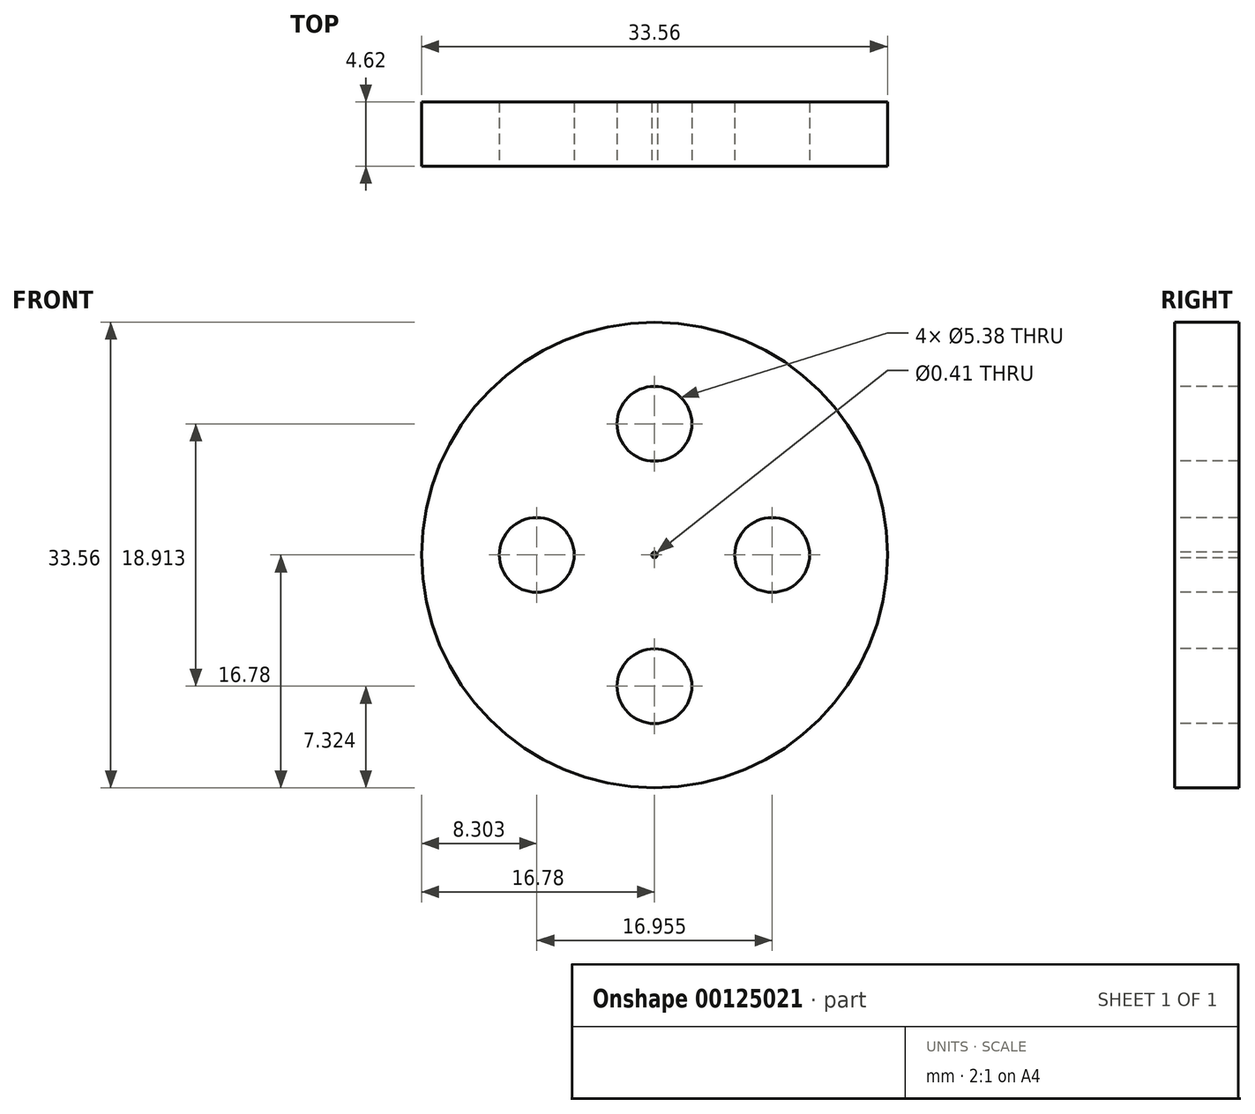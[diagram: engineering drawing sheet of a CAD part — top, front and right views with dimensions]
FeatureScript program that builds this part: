
annotation { "Feature Type Name" : "Feature", "Feature Type Description" : "" }
export const myFeature = defineFeature(function(context is Context, id is Id, definition is map)
    precondition{}
    {
        {
            var Q0;
            Q0=qCreatedBy(makeId("Front.planeOp"),FACE);
            var sketch = newSketch(context, id + "F0", { "sketchPlane" : qUnion([Q0])});
            skCircle(sketch, "E0", {"center": v(0, 0) * mm, "radius": 16.78 * mm});
            skCircle(sketch, "E1", {"center": v(0, 0) * mm, "radius": 0.2 * mm});
            skCircle(sketch, "E2", {"center": v(0, 9.46) * mm, "radius": 2.7 * mm});
            skCircle(sketch, "E3", {"center": v(0, -9.46) * mm, "radius": 2.7 * mm});
            skCircle(sketch, "E4", {"center": v(8.48, 0) * mm, "radius": 2.7 * mm});
            skCircle(sketch, "E5", {"center": v(-8.48, 0) * mm, "radius": 2.7 * mm});
            skSolve(sketch);
        }
        {
            var Q0;
            Q0=qCreatedBy(makeId("Right.planeOp"),FACE);
            var sketch = newSketch(context, id + "F1", { "sketchPlane" : qUnion([Q0])});
            skLineSegment(sketch, "E6", {"start": v(-2.95, 8.4) * mm, "end": v(1.67, 8.4) * mm});
            skSolve(sketch);
        }
        {
            var Q0;
            Q0=makeQuery(id+"F0.imprint","IMPRINT",FACE,{"disambiguationData":[TD([[makeQuery(id+"F0.imprint","IMPRINT",EDGE,{"derivedFrom":sQuery(id+"F0.wireOp",EDGE,"E0")}),1.0]])]});
            var Q1;
            Q1=sQuery(id+"F1.wireOp",EDGE,"E6");
            sweep(context, id + "F2", {"profiles" : qUnion([Q0]), "path" : qUnion([Q1])});
        }
    });
